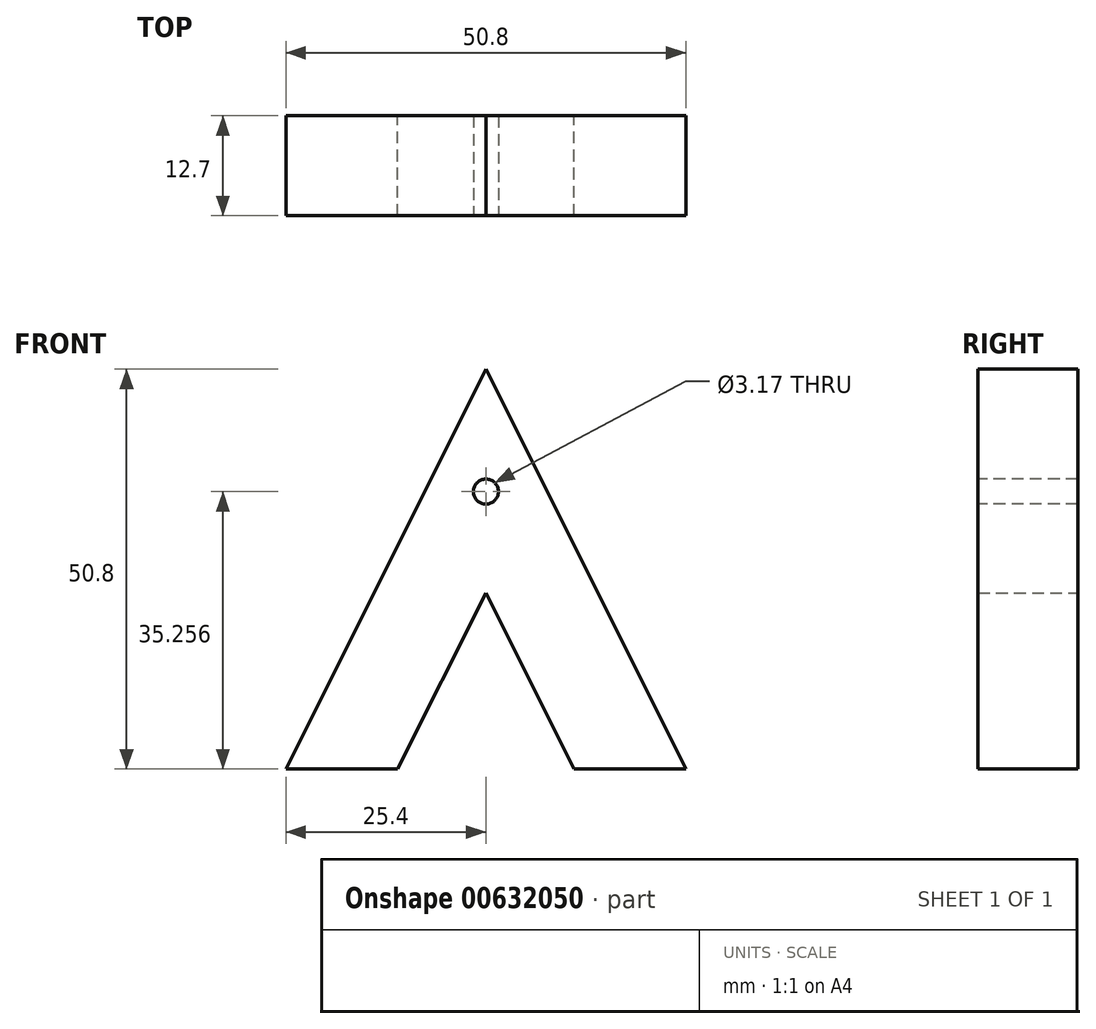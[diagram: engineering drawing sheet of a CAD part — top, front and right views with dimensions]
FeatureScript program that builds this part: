
annotation { "Feature Type Name" : "Feature", "Feature Type Description" : "" }
export const myFeature = defineFeature(function(context is Context, id is Id, definition is map)
    precondition{}
    {
        {
            var Q0;
            Q0=qCreatedBy(makeId("Front.planeOp"),FACE);
            var sketch = newSketch(context, id + "F0", { "sketchPlane" : qUnion([Q0])});
            skLineSegment(sketch, "E0", {"start": v(0, 0) * mm, "end": v(25.4, 50.8) * mm});
            skLineSegment(sketch, "E1", {"start": v(25.4, 50.8) * mm, "end": v(50.8, 0) * mm});
            skLineSegment(sketch, "E2", {"start": v(50.8, 0) * mm, "end": v(36.6, 0) * mm});
            skLineSegment(sketch, "E3", {"start": v(36.6, 0) * mm, "end": v(25.4, 22.4) * mm});
            skLineSegment(sketch, "E4", {"start": v(25.4, 22.4) * mm, "end": v(14.2, 0) * mm});
            skLineSegment(sketch, "E5", {"start": v(14.2, 0) * mm, "end": v(0, 0) * mm});
            skSolve(sketch);
        }
        {
            var Q0;
            Q0 = qSketchRegion(id + "F0", true);
            extrude(context, id + "F1", {"entities" : qUnion([Q0]), "depth" : 12.7 * mm, "offsetDistance" : 25.4 * mm});
        }
        {
            var Q0;
            Q0=makeQuery(id+"F1.opExtrude","CAP_FACE",FACE,{"disambiguationData":[OSD([sQuery(id+"F0.wireOp",EDGE,"E0"),sQuery(id+"F0.wireOp",EDGE,"E1"),sQuery(id+"F0.wireOp",EDGE,"E2"),sQuery(id+"F0.wireOp",EDGE,"E3"),sQuery(id+"F0.wireOp",EDGE,"E4"),sQuery(id+"F0.wireOp",EDGE,"E5")])],"isStart":false});
            var sketch = newSketch(context, id + "F2", { "sketchPlane" : qUnion([Q0])});
            skCircle(sketch, "E6", {"center": v(25.4, 35.26) * mm, "radius": 1.59 * mm});
            skSolve(sketch);
        }
        {
            var Q0;
            Q0 = qSketchRegion(id + "F2", true);
            extrude(context, id + "F3", {"entities" : qUnion([Q0]), "operationType" : NewBodyOperationType.REMOVE, "oppositeDirection" : true, "depth" : 25.4 * mm, "offsetDistance" : 25.4 * mm});
        }
    });
